# Revit family: IS_ConnectAir_Multiproduct_BIM_DE_E1134;E1135
name_source: partatom
category: Plumbing Fixtures
revit_build: Autodesk Revit MEP 2014 (Build: 20130308_1515(x64)
units: mm (PartAtom-declared; Revit-internal decimal feet)

## types (2) — shared parameters
Accessories = www.idealstandard.de\ersatzteile
AreaUnits = millimeters
Assembly Code = C1030200
AssetType = Fixed
BathType = Domestic
Brand = Ideal Standard
Category = SanitaryTerminal_BATH_DE
CodePerformance = DIN EN 14516, DIN EN 232, DIN EN 198
Color = white
ConnectionType = Plumbing
Default Elevation = 550 mm
DrainSize = 52 mm
DurationUnit = year
ExpectedLife = 25
Features = Connect Air shower bath tub
Finish = white
GrossWeight = 0
HasGrabHandles = No
IfcExportAs = IfcSanitaryTerminalType
IfcExportType = BATH
InstallationInstructions = www.idealstandard.de\produkte
LinearUnits = millimeters
ManufacturerURL = www.idealstandard.de
Material = Sanitary Brass
MaterialThickness = 4 mm  [stored 0.0131234 ft]
NBSDescription = Baths
NBSReference = 45-35-70/311
NettWeight = 28,5 kg
NominalHeight = 400 mm  [stored 1.31234 ft]
NominalLength = 1695 mm
NominalWidth = 795 mm
ProductInformation = www.idealstandard.de/produkte
Shape = Rectangular
Size = 1700x800x465mm
Space = Internal
SpareParts = www.idealstandard.de/ersatzteile
TMV3 = No
URL = www.idealstandard.com
Uniclass2015Code = Pr_40_20_06_08
Uniclass2015Title = Baths
Uniclass2015Version = Products v1.1
Version = 1
VolumeUnits = Litres
WarrantyDescription = Manufacturers Warranty
WarrantyDurationUnit = year
zero-valued in all types: NominalDepth

## per-type parameters (varying)
| type | BIMObjectName | BarCode | Description | Model | ModelNumber | ModelReference | Name | e1134 | e1135 |
| E113401 - Connect Air shower bath tub - right hand | ISI_IdealStandard_Baths_ConnectAir_E113401 | 5017830518853 | E113401 Connect Air shower bath tub | E113401 | E113401 | E113401 Connect Air shower bath tub | Baths_ConnectAir_E113401_IdealStandard | Yes | No |
| E113501 - Connect Air shower bath tub - left hand | ISI_IdealStandard_Baths_ConnectAir_E113501 | 5017830518860 | E113501 Connect Air shower bath tub | E113501 | E113501 | E113501 Connect Air shower bath tub | Baths_ConnectAir_E113501_IdealStandard | No | Yes |

note: [stored X ft] marks values corroborated as IEEE doubles in the binary element streams (Revit-internal decimal feet)

## geometry (parser evidence)
native form markers: Sweep x3
no freeform markers — native parametric forms only
